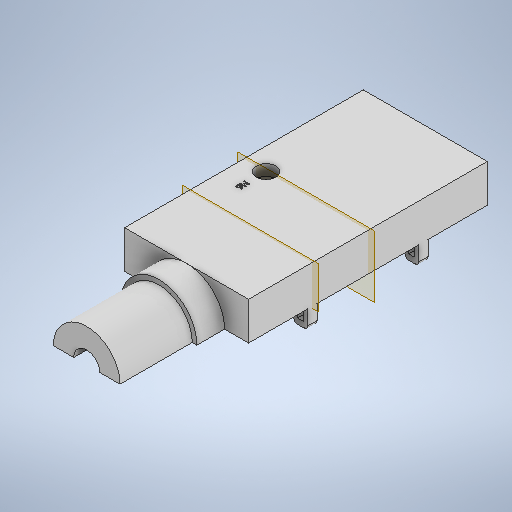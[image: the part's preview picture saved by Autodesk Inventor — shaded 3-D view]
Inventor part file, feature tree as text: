
AUTODESK INVENTOR PART (.ipt)
format: ipt  version: 2025 (Build 290162000, 162)  size: 378,880 bytes
history: native  units: mm
features: sketch x7, extrude x5, plane x1, mirror x1, hole x1, emboss x1
ambient origin geometry x8: Origin, YZ Plane, XZ Plane, XY Plane, X Axis, Y Axis, Z Axis, Center Point
bodies: Solid1 (feature_tree)
feature tree (16):
  extrude  "Extrusion1"  Depth=20.5mm
  extrude  "Extrusion2"  Depth=20.5mm
  extrude  "Extrusion3"  Depth=18.0mm
  extrude  "Extrusion5"  Depth=39.0mm TaperAngle=0.0deg
  plane  "Work Plane1"
  extrude  "Extrusion6"  TaperAngle=180.0deg  [1 undecoded]
  mirror  "Mirror1"
  hole  "Hole1"  [1 undecoded]
  emboss  "Emboss1"
  sketch  "Sketch1"  dims[d0=129.0mm d1=20.5mm]
  sketch  "Sketch2"  dims[d2=67.0mm d3=0.0mm d4=20.5mm]
  sketch  "Sketch3"  dims[d5=15.0mm d6=0.0mm d7=18.0mm]
  sketch  "Sketch5"  dims[d8=180.0deg d9=39.0mm d10=0.0mm]
  sketch  "Sketch6"  dims[d16=7.0mm d17=180.0deg]
  sketch  "Sketch7"  dims[d18=0.0mm d19=0.0mm d20=30.0mm]
  sketch  "Sketch8"  dims[d21=10.0mm d22=2.5mm d23=7.0mm d24=7.5mm d25=5.0mm d26=2.0mm d27=2.0mm d28=2.0mm d29=5.0mm d30=0.0mm d31=6.2mm d32=6.0mm d33=10.5mm d34=6.0mm d35=90.0deg d36=8.0mm d37=20.594885mm d38=12.0mm d39=1.0mm d40=0.0mm]
note: 2 required parameter values undecoded (feature->parameter linkage not recoverable at this tier; creation-order binding heuristic only, values carry confidence <= 0.55)
